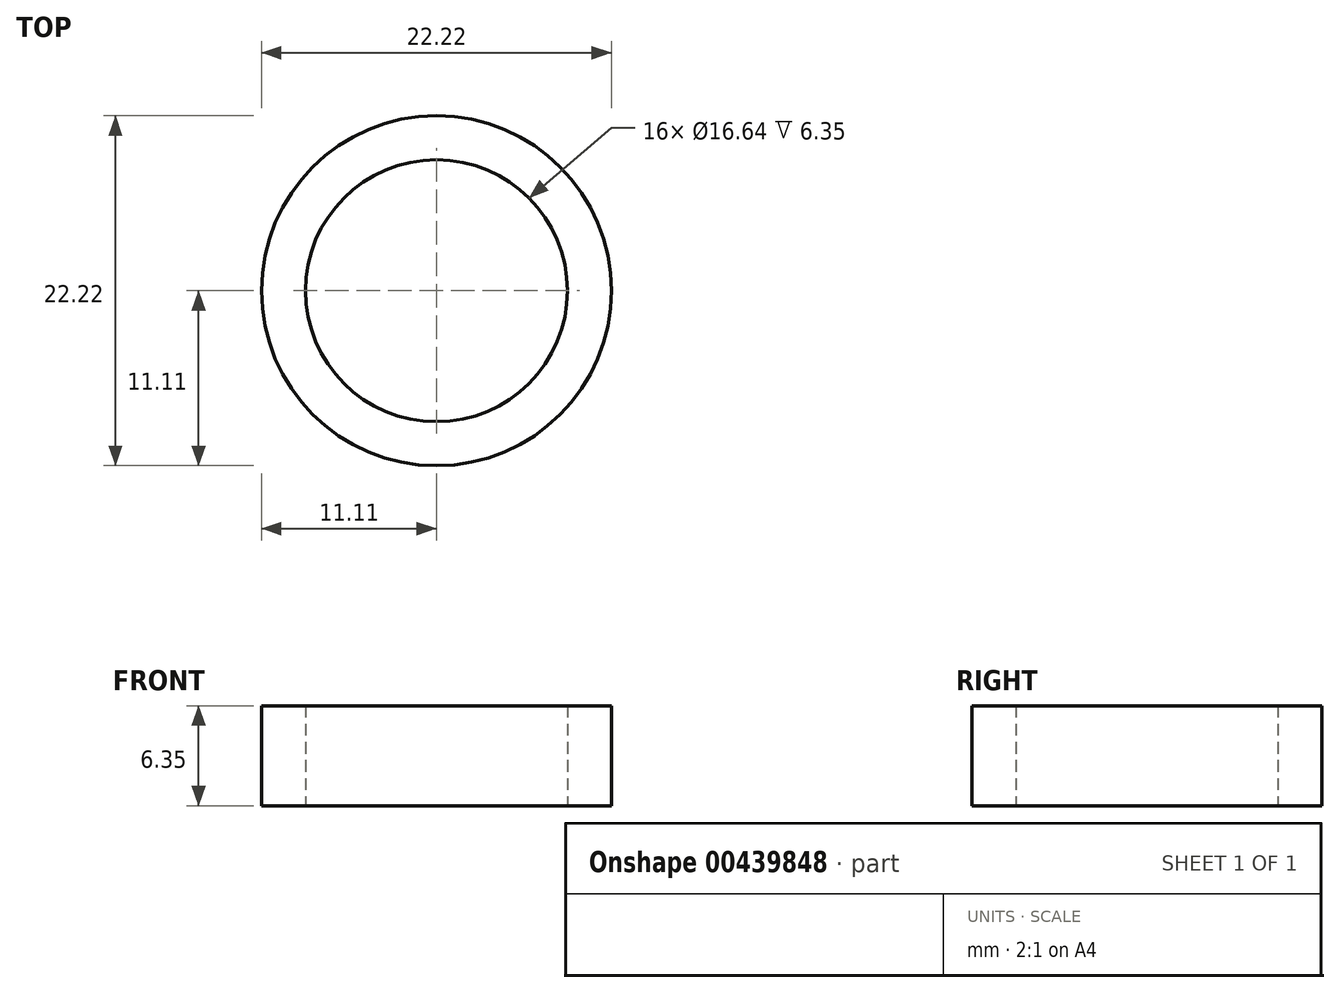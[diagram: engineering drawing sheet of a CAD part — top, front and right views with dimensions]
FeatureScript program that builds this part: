
annotation { "Feature Type Name" : "Feature", "Feature Type Description" : "" }
export const myFeature = defineFeature(function(context is Context, id is Id, definition is map)
    precondition{}
    {
        {
            var Q0;
            Q0=qCreatedBy(makeId("Top.planeOp"),FACE);
            var sketch = newSketch(context, id + "F0", { "sketchPlane" : qUnion([Q0])});
            skCircle(sketch, "E0", {"center": v(0, 0) * mm, "radius": 8.32 * mm});
            skCircle(sketch, "E1", {"center": v(0, 0) * mm, "radius": 11.11 * mm});
            skSolve(sketch);
        }
        {
            var Q0;
            Q0=makeQuery(id+"F0.imprint","IMPRINT",FACE,{"disambiguationData":[TD([[makeQuery(id+"F0.imprint","IMPRINT",EDGE,{"derivedFrom":sQuery(id+"F0.wireOp",EDGE,"E0")}),-1.0]])]});
            extrude(context, id + "F1", {"entities" : qUnion([Q0]), "depth" : 6.35 * mm});
        }
    });
